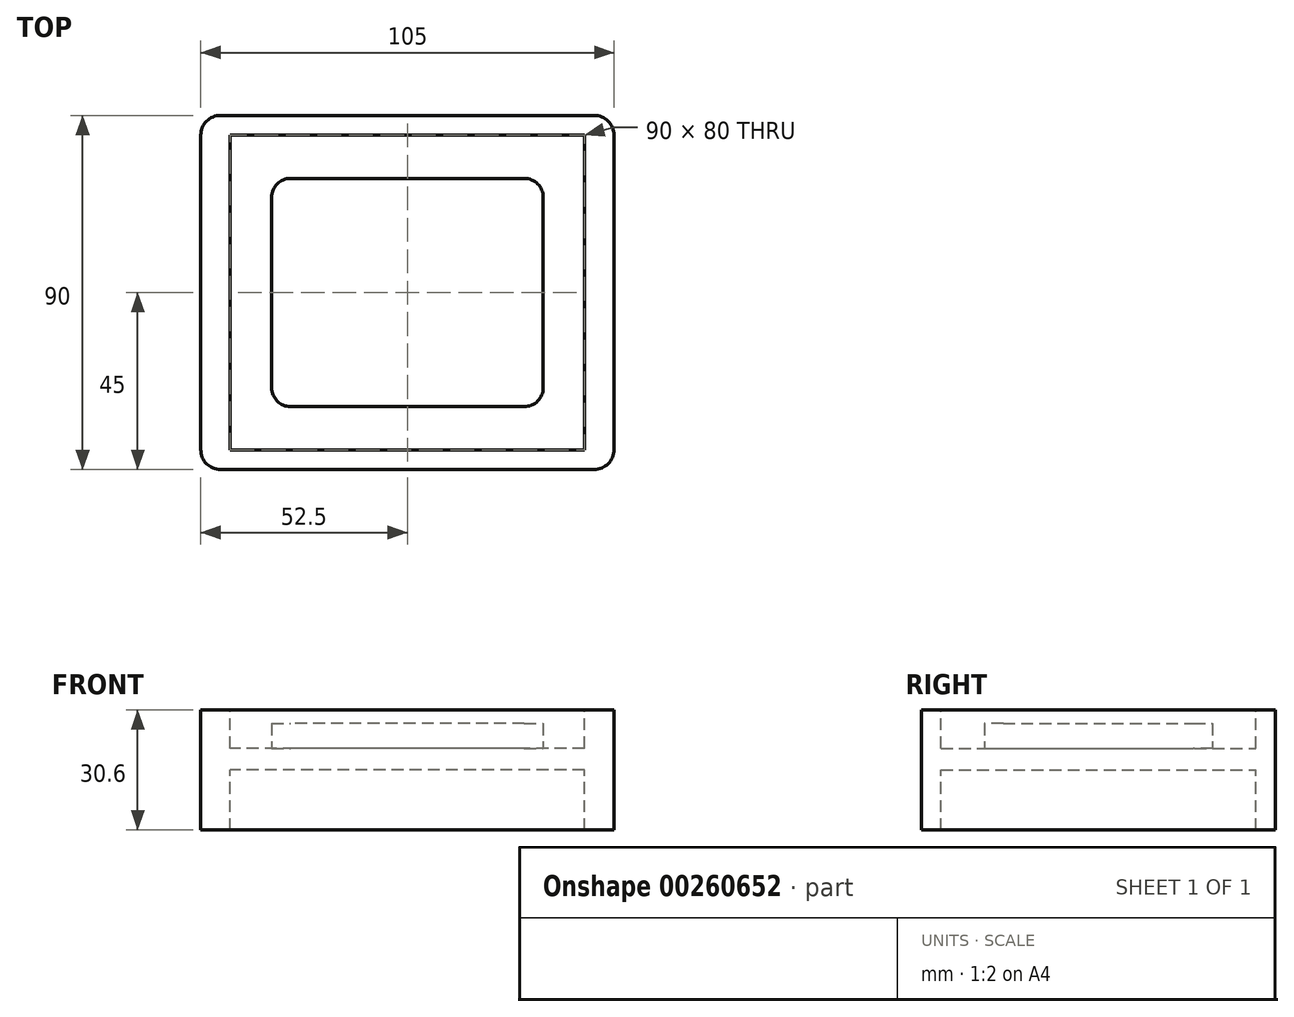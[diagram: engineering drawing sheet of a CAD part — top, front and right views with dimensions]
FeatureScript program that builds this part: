
annotation { "Feature Type Name" : "Feature", "Feature Type Description" : "" }
export const myFeature = defineFeature(function(context is Context, id is Id, definition is map)
    precondition{}
    {
        {
            var Q0;
            Q0=qCreatedBy(makeId("Top.planeOp"),FACE);
            var sketch = newSketch(context, id + "F0", { "sketchPlane" : qUnion([Q0])});
            skLineSegment(sketch, "E0.bottom", {"start": v(52.5, -45) * mm, "end": v(-52.5, -45) * mm});
            skLineSegment(sketch, "E0.top", {"start": v(52.5, 45) * mm, "end": v(-52.5, 45) * mm});
            skLineSegment(sketch, "E0.left", {"start": v(52.5, -45) * mm, "end": v(52.5, 45) * mm});
            skLineSegment(sketch, "E0.right", {"start": v(-52.5, -45) * mm, "end": v(-52.5, 45) * mm});
            skPoint(sketch, "E0.middle", {"position": v(0, 0) * mm});
            skLineSegment(sketch, "E1.bottom", {"start": v(45, -40) * mm, "end": v(-45, -40) * mm});
            skLineSegment(sketch, "E1.top", {"start": v(45, 40) * mm, "end": v(-45, 40) * mm});
            skLineSegment(sketch, "E1.left", {"start": v(45, -40) * mm, "end": v(45, 40) * mm});
            skLineSegment(sketch, "E1.right", {"start": v(-45, -40) * mm, "end": v(-45, 40) * mm});
            skLineSegment(sketch, "E2.bottom", {"start": v(34.5, -29) * mm, "end": v(-34.5, -29) * mm});
            skLineSegment(sketch, "E2.top", {"start": v(34.5, 29) * mm, "end": v(-34.5, 29) * mm});
            skLineSegment(sketch, "E2.left", {"start": v(34.5, -29) * mm, "end": v(34.5, 29) * mm});
            skLineSegment(sketch, "E2.right", {"start": v(-34.5, -29) * mm, "end": v(-34.5, 29) * mm});
            skSolve(sketch);
        }
        {
            var Q0;
            Q0=makeQuery(id+"F0.imprint","IMPRINT",FACE,{"disambiguationData":[TD([[makeQuery(id+"F0.imprint","IMPRINT",EDGE,{"derivedFrom":sQuery(id+"F0.wireOp",EDGE,"E0.bottom")}),-1.0]])]});
            extrude(context, id + "F1", {"entities" : qUnion([Q0]), "endBound" : BoundingType.SYMMETRIC, "oppositeDirection" : true, "depth" : 30.6 * mm});
        }
        {
            var Q0;
            {var subQ0=sQuery(id+"F0.wireOp",EDGE,"E0.right");var subQ1=sQuery(id+"F0.wireOp",EDGE,"E0.bottom");Q0=makeQuery(id+"FCIbbEiRGQ69zdl_0.boolean.opBoolean","MERGE",EDGE,{"derivedFrom":[makeQuery(id+"F1.opExtrude","SWEPT_EDGE",EDGE,{"disambiguationData":[OSD([subQ1,subQ0])]}),makeQuery(id+"FCIbbEiRGQ69zdl_0.opExtrude","SWEPT_EDGE",EDGE,{"disambiguationData":[OSD([subQ1,subQ0])]})]});}
            var Q1;
            {var subQ0=sQuery(id+"F0.wireOp",EDGE,"E0.right");var subQ1=sQuery(id+"F0.wireOp",EDGE,"E0.top");Q1=makeQuery(id+"FCIbbEiRGQ69zdl_0.boolean.opBoolean","MERGE",EDGE,{"derivedFrom":[makeQuery(id+"F1.opExtrude","SWEPT_EDGE",EDGE,{"disambiguationData":[OSD([subQ1,subQ0])]}),makeQuery(id+"FCIbbEiRGQ69zdl_0.opExtrude","SWEPT_EDGE",EDGE,{"disambiguationData":[OSD([subQ1,subQ0])]})]});}
            var Q2;
            {var subQ0=sQuery(id+"F0.wireOp",EDGE,"E0.left");var subQ1=sQuery(id+"F0.wireOp",EDGE,"E0.bottom");Q2=makeQuery(id+"FCIbbEiRGQ69zdl_0.boolean.opBoolean","MERGE",EDGE,{"derivedFrom":[makeQuery(id+"F1.opExtrude","SWEPT_EDGE",EDGE,{"disambiguationData":[OSD([subQ1,subQ0])]}),makeQuery(id+"FCIbbEiRGQ69zdl_0.opExtrude","SWEPT_EDGE",EDGE,{"disambiguationData":[OSD([subQ1,subQ0])]})]});}
            var Q3;
            {var subQ0=sQuery(id+"F0.wireOp",EDGE,"E0.left");var subQ1=sQuery(id+"F0.wireOp",EDGE,"E0.top");Q3=makeQuery(id+"FCIbbEiRGQ69zdl_0.boolean.opBoolean","MERGE",EDGE,{"derivedFrom":[makeQuery(id+"F1.opExtrude","SWEPT_EDGE",EDGE,{"disambiguationData":[OSD([subQ1,subQ0])]}),makeQuery(id+"FCIbbEiRGQ69zdl_0.opExtrude","SWEPT_EDGE",EDGE,{"disambiguationData":[OSD([subQ1,subQ0])]})]});}
            fillet(context, id + "F2", {"entities" : qUnion([Q0, Q1, Q2, Q3]), "radius" : 5.07 * mm, "tangentPropagation" : true, "allowEdgeOverflow" : false});
        }
        {
            var Q0;
            Q0=makeQuery(id+"F0.imprint","IMPRINT",FACE,{"disambiguationData":[TD([[makeQuery(id+"F0.imprint","IMPRINT",EDGE,{"derivedFrom":sQuery(id+"F0.wireOp",EDGE,"E1.bottom")}),-1.0]])]});
            extrude(context, id + "F3", {"entities" : qUnion([Q0]), "operationType" : NewBodyOperationType.ADD, "depth" : 5.5 * mm});
        }
        {
            var Q0;
            Q0=makeQuery(id+"F0.imprint","IMPRINT",FACE,{"disambiguationData":[TD([[makeQuery(id+"F0.imprint","IMPRINT",EDGE,{"derivedFrom":sQuery(id+"F0.wireOp",EDGE,"E2.bottom")}),-1.0]])]});
            extrude(context, id + "F4", {"entities" : qUnion([Q0]), "operationType" : NewBodyOperationType.ADD, "depth" : 11.8 * mm});
        }
        {
            var Q0;
            Q0=makeQuery(id+"F4.opExtrude","SWEPT_EDGE",EDGE,{"disambiguationData":[OSD([sQuery(id+"F0.wireOp",EDGE,"E2.bottom"),sQuery(id+"F0.wireOp",EDGE,"E2.left")])]});
            var Q1;
            Q1=makeQuery(id+"F4.opExtrude","SWEPT_EDGE",EDGE,{"disambiguationData":[OSD([sQuery(id+"F0.wireOp",EDGE,"E2.top"),sQuery(id+"F0.wireOp",EDGE,"E2.left")])]});
            var Q2;
            Q2=makeQuery(id+"F4.opExtrude","SWEPT_EDGE",EDGE,{"disambiguationData":[OSD([sQuery(id+"F0.wireOp",EDGE,"E2.top"),sQuery(id+"F0.wireOp",EDGE,"E2.right")])]});
            var Q3;
            Q3=makeQuery(id+"F4.opExtrude","SWEPT_EDGE",EDGE,{"disambiguationData":[OSD([sQuery(id+"F0.wireOp",EDGE,"E2.bottom"),sQuery(id+"F0.wireOp",EDGE,"E2.right")])]});
            fillet(context, id + "F5", {"entities" : qUnion([Q0, Q1, Q2, Q3]), "radius" : 4.83 * mm, "tangentPropagation" : true, "allowEdgeOverflow" : false});
        }
    });
